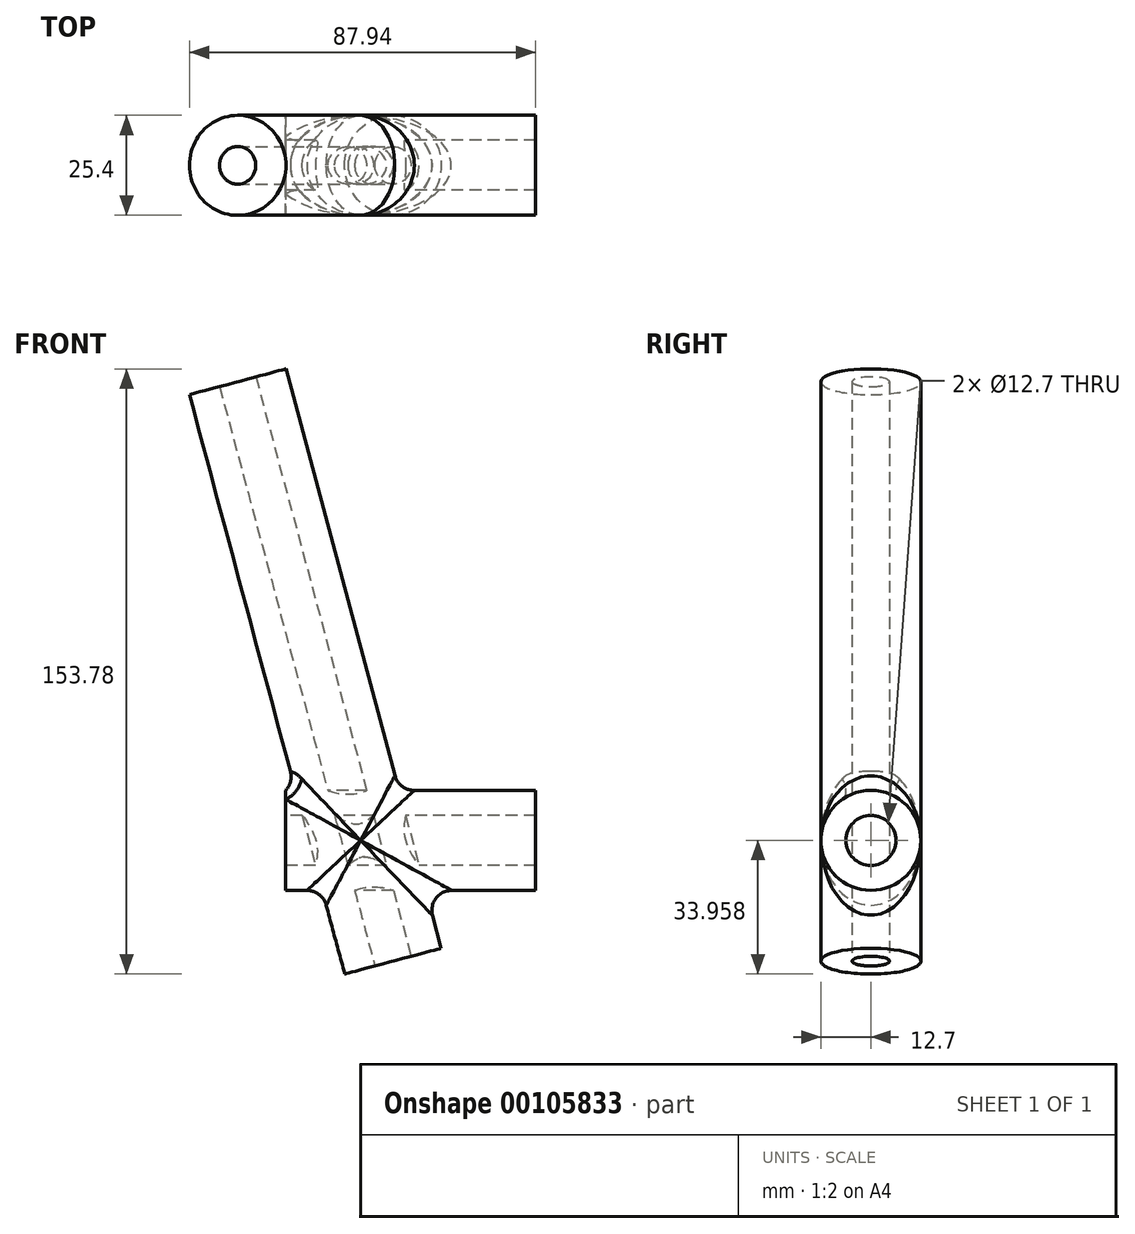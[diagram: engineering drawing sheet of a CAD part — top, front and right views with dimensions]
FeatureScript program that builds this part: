
annotation { "Feature Type Name" : "Feature", "Feature Type Description" : "" }
export const myFeature = defineFeature(function(context is Context, id is Id, definition is map)
    precondition{}
    {
        {
            var Q0;
            Q0=qCreatedBy(makeId("Front.planeOp"),FACE);
            var sketch = newSketch(context, id + "F0", { "sketchPlane" : qUnion([Q0])});
            skLineSegment(sketch, "E0", {"start": v(0, 0) * mm, "end": v(-39.44, 147.2) * mm, "construction": true});
            skLineSegment(sketch, "E1", {"start": v(-39.44, 147.2) * mm, "end": v(-27.18, 150.5) * mm});
            skLineSegment(sketch, "E2", {"start": v(0, 0) * mm, "end": v(12.27, 3.29) * mm});
            skLineSegment(sketch, "E3", {"start": v(-27.18, 150.5) * mm, "end": v(12.27, 3.29) * mm});
            skLineSegment(sketch, "E4.MirrorCS", {"start": v(-39.44, 147.2) * mm, "end": v(-51.71, 143.92) * mm});
            skLineSegment(sketch, "E5.MirrorCS", {"start": v(-51.71, 143.92) * mm, "end": v(-12.27, -3.29) * mm});
            skLineSegment(sketch, "E6.MirrorCS", {"start": v(0, 0) * mm, "end": v(-12.27, -3.29) * mm});
            skPoint(sketch, "E7", {"position": v(-32.87, 122.67) * mm});
            skPoint(sketch, "E8", {"position": v(-8.22, 30.67) * mm});
            skLineSegment(sketch, "E9", {"start": v(-27.27, 30.67) * mm, "end": v(42.58, 30.67) * mm, "construction": true});
            skLineSegment(sketch, "E10", {"start": v(0, 0) * mm, "end": v(0, 154.84) * mm, "construction": true});
            skLineSegment(sketch, "E11", {"start": v(-34.84, 148.44) * mm, "end": v(4.6, 1.23) * mm});
            skLineSegment(sketch, "E12.MirrorCS", {"start": v(-44.04, 145.97) * mm, "end": v(-4.6, -1.23) * mm});
            skSolve(sketch);
        }
        {
            var Q0;
            {var subQ0=sQuery(id+"F0.wireOp",EDGE,"E3");var subQ1=sQuery(id+"F0.wireOp",EDGE,"E1");var subQ2=makeQuery(id+"F0.imprint","INTERSECT",VERTEX,{"derivedFrom":[subQ1,subQ0]});Q0=makeQuery(id+"F0.imprint","IMPRINT",FACE,{"disambiguationData":[TD([[makeQuery(id+"F0.imprint","IMPRINT",EDGE,{"disambiguationData":[TD([[subQ2,1.0]])],"derivedFrom":subQ1}),-1.0]])]});}
            var Q1;
            {var subQ0=sQuery(id+"F0.wireOp",EDGE,"gSkgpmrd-mNum-AWEB-XdBQ-kxS4PibQjmh7");var subQ1=sQuery(id+"F0.wireOp",EDGE,"E3");var subQ2=makeQuery(id+"F0.imprint","INTERSECT",VERTEX,{"derivedFrom":[subQ1,subQ0]});Q1=makeQuery(id+"F0.imprint","IMPRINT",FACE,{"disambiguationData":[TD([[makeQuery(id+"F0.imprint","IMPRINT",EDGE,{"disambiguationData":[TD([[subQ2,-1.0]])],"derivedFrom":subQ1}),-1.0]])]});}
            var Q2;
            {var subQ0=sQuery(id+"F0.wireOp",EDGE,"OIvqEEVQ-YJRY-AYzA-Em1w-y26UKtvZ7IGO");var subQ1=sQuery(id+"F0.wireOp",EDGE,"E3");var subQ2=makeQuery(id+"F0.imprint","INTERSECT",VERTEX,{"derivedFrom":[subQ1,subQ0]});Q2=makeQuery(id+"F0.imprint","IMPRINT",FACE,{"disambiguationData":[TD([[makeQuery(id+"F0.imprint","IMPRINT",EDGE,{"disambiguationData":[TD([[subQ2,-1.0]])],"derivedFrom":subQ1}),-1.0]])]});}
            var Q3;
            {var subQ0=sQuery(id+"F0.wireOp",EDGE,"bd3d5c77-a280-4ef9-8ed5-a5b15724989e0.MirrorCS");var subQ1=sQuery(id+"F0.wireOp",EDGE,"E3");var subQ2=makeQuery(id+"F0.imprint","INTERSECT",VERTEX,{"derivedFrom":[subQ1,subQ0]});Q3=makeQuery(id+"F0.imprint","IMPRINT",FACE,{"disambiguationData":[TD([[makeQuery(id+"F0.imprint","IMPRINT",EDGE,{"disambiguationData":[TD([[subQ2,1.0]])],"derivedFrom":subQ1}),-1.0]])]});}
            var Q4;
            {var subQ0=sQuery(id+"F0.wireOp",EDGE,"E3");var subQ1=sQuery(id+"F0.wireOp",EDGE,"E2");var subQ2=makeQuery(id+"F0.imprint","INTERSECT",VERTEX,{"derivedFrom":[subQ1,subQ0]});Q4=makeQuery(id+"F0.imprint","IMPRINT",FACE,{"disambiguationData":[TD([[makeQuery(id+"F0.imprint","IMPRINT",EDGE,{"disambiguationData":[TD([[subQ2,1.0]])],"derivedFrom":subQ1}),1.0]])]});}
            var Q5;
            Q5=sQuery(id+"F0.wireOp",EDGE,"E0");
            revolve(context, id + "F1", {"entities" : qUnion([Q0, Q1, Q2, Q3, Q4]), "axis" : qUnion([Q5]), "revolveType" : RevolveType.FULL});
        }
        {
            var Q0;
            Q0=qCreatedBy(makeId("Front.planeOp"),FACE);
            var sketch = newSketch(context, id + "F2", { "sketchPlane" : qUnion([Q0])});
            skLineSegment(sketch, "E13.bottom", {"start": v(36.23, 37.02) * mm, "end": v(-27.27, 37.02) * mm});
            skLineSegment(sketch, "E13.top", {"start": v(36.23, 43.37) * mm, "end": v(-27.27, 43.37) * mm});
            skLineSegment(sketch, "E13.left", {"start": v(36.23, 37.02) * mm, "end": v(36.23, 43.37) * mm});
            skLineSegment(sketch, "E13.right", {"start": v(-27.27, 37.02) * mm, "end": v(-27.27, 43.37) * mm});
            skSolve(sketch);
        }
        {
            var Q0;
            Q0 = qSketchRegion(id + "F2", true);
            var Q1;
            Q1=sQuery(id+"F0.wireOp",EDGE,"E9");
            revolve(context, id + "F3", {"operationType" : NewBodyOperationType.ADD, "entities" : qUnion([Q0]), "axis" : qUnion([Q1]), "revolveType" : RevolveType.FULL});
        }
        {
            var Q0;
            Q0=makeQuery(id+"F3.boolean.opBoolean","INTERSECT",EDGE,{"disambiguationData":[OD(0.0)],"derivedFrom":[makeQuery(id+"F1.opRevolve","SWEPT_FACE",FACE,{"disambiguationData":[OSD([sQuery(id+"F0.wireOp",EDGE,"E3")])]}),makeQuery(id+"F3.opRevolve","SWEPT_FACE",FACE,{"disambiguationData":[OSD([sQuery(id+"F2.wireOp",EDGE,"E13.top")])]})]});
            var Q1;
            Q1=makeQuery(id+"F3.boolean.opBoolean","INTERSECT",EDGE,{"disambiguationData":[OD(1.0)],"derivedFrom":[makeQuery(id+"F1.opRevolve","SWEPT_FACE",FACE,{"disambiguationData":[OSD([sQuery(id+"F0.wireOp",EDGE,"E3")])]}),makeQuery(id+"F3.opRevolve","SWEPT_FACE",FACE,{"disambiguationData":[OSD([sQuery(id+"F2.wireOp",EDGE,"E13.top")])]})]});
            var Q2;
            Q2=makeQuery(id+"F3.boolean.opBoolean","INTERSECT",EDGE,{"disambiguationData":[OD(3.0)],"derivedFrom":[makeQuery(id+"F1.opRevolve","SWEPT_FACE",FACE,{"disambiguationData":[OSD([sQuery(id+"F0.wireOp",EDGE,"E3")])]}),makeQuery(id+"F3.opRevolve","SWEPT_FACE",FACE,{"disambiguationData":[OSD([sQuery(id+"F2.wireOp",EDGE,"E13.top")])]})]});
            var Q3;
            Q3=makeQuery(id+"F3.boolean.opBoolean","INTERSECT",EDGE,{"disambiguationData":[OD(2.0)],"derivedFrom":[makeQuery(id+"F1.opRevolve","SWEPT_FACE",FACE,{"disambiguationData":[OSD([sQuery(id+"F0.wireOp",EDGE,"E3")])]}),makeQuery(id+"F3.opRevolve","SWEPT_FACE",FACE,{"disambiguationData":[OSD([sQuery(id+"F2.wireOp",EDGE,"E13.top")])]})]});
            fillet(context, id + "F4", {"entities" : qUnion([Q0, Q1, Q2, Q3]), "radius" : 5.08 * mm, "tangentPropagation" : true, "allowEdgeOverflow" : false});
        }
    });
